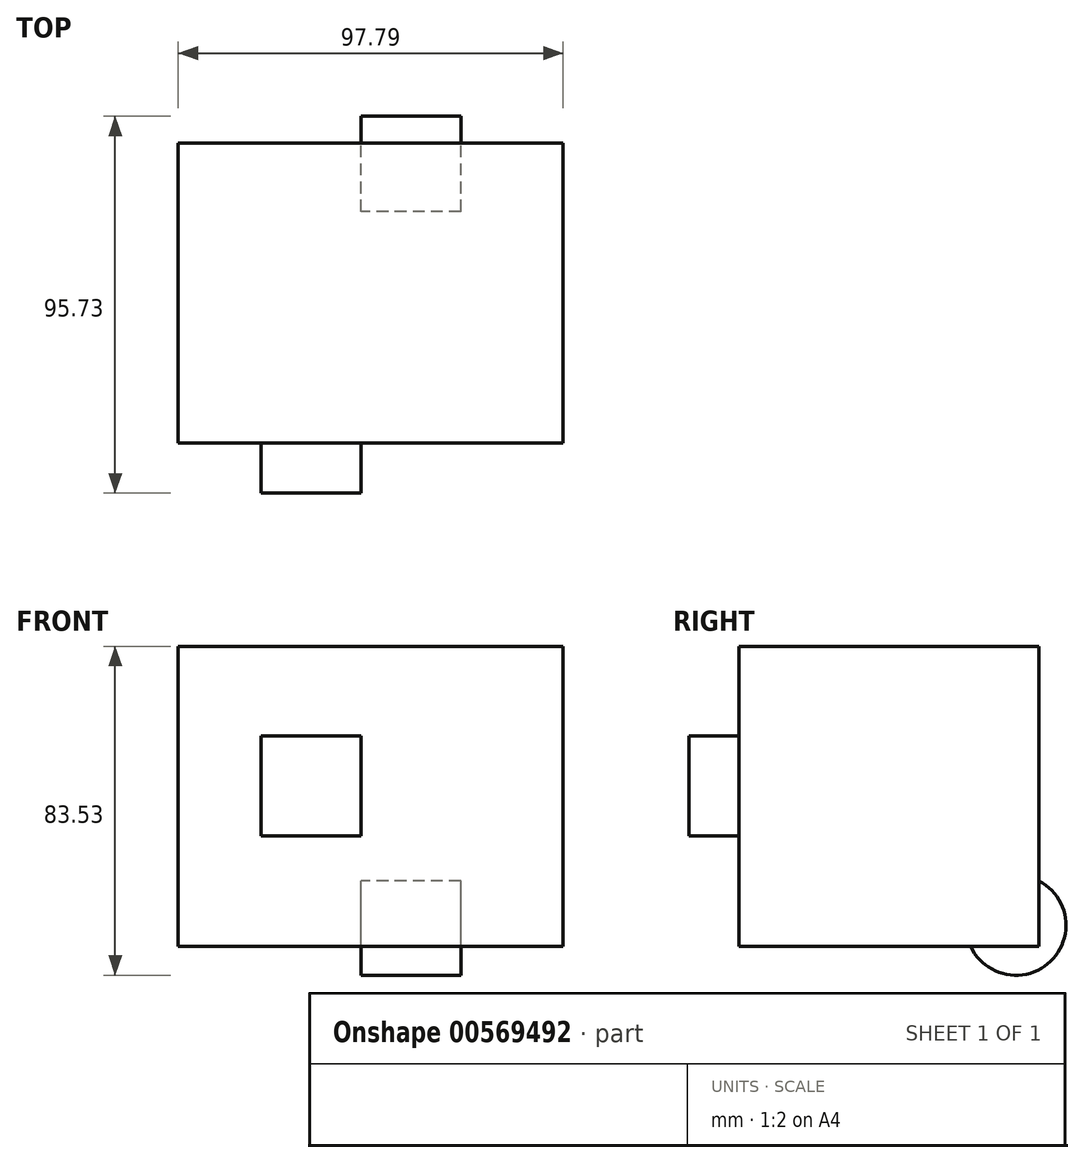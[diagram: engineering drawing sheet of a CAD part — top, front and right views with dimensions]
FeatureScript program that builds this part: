
annotation { "Feature Type Name" : "Feature", "Feature Type Description" : "" }
export const myFeature = defineFeature(function(context is Context, id is Id, definition is map)
    precondition{}
    {
        {
            var Q0;
            Q0=qCreatedBy(makeId("Front.planeOp"),FACE);
            var sketch = newSketch(context, id + "F0", { "sketchPlane" : qUnion([Q0])});
            skLineSegment(sketch, "E0.bottom", {"start": v(-53.9, 110.26) * mm, "end": v(22.3, 110.26) * mm});
            skLineSegment(sketch, "E0.top", {"start": v(-53.9, 34.06) * mm, "end": v(22.3, 34.06) * mm});
            skLineSegment(sketch, "E0.left", {"start": v(-53.9, 110.26) * mm, "end": v(-53.9, 34.06) * mm});
            skLineSegment(sketch, "E0.right", {"start": v(22.3, 110.26) * mm, "end": v(22.3, 34.06) * mm});
            skSolve(sketch);
        }
        {
            var Q0;
            Q0 = qSketchRegion(id + "F0", true);
            extrude(context, id + "F1", {"entities" : qUnion([Q0]), "depth" : 76.2 * mm, "offsetDistance" : 25.4 * mm});
        }
        {
            var Q0;
            Q0=makeQuery(id+"F1.opExtrude","CAP_FACE",FACE,{"disambiguationData":[OSD([sQuery(id+"F0.wireOp",EDGE,"E0.bottom"),sQuery(id+"F0.wireOp",EDGE,"E0.top"),sQuery(id+"F0.wireOp",EDGE,"E0.left"),sQuery(id+"F0.wireOp",EDGE,"E0.right")])],"isStart":false});
            var sketch = newSketch(context, id + "F2", { "sketchPlane" : qUnion([Q0])});
            skLineSegment(sketch, "E1.bottom", {"start": v(-32.92, 87.51) * mm, "end": v(-7.52, 87.51) * mm});
            skLineSegment(sketch, "E1.top", {"start": v(-32.92, 62.11) * mm, "end": v(-7.52, 62.11) * mm});
            skLineSegment(sketch, "E1.left", {"start": v(-32.92, 87.51) * mm, "end": v(-32.92, 62.11) * mm});
            skLineSegment(sketch, "E1.right", {"start": v(-7.52, 87.51) * mm, "end": v(-7.52, 62.11) * mm});
            skSolve(sketch);
        }
        {
            var Q0;
            Q0=makeQuery(id+"F2.imprint","IMPRINT",FACE,{"disambiguationData":[TD([[makeQuery(id+"F2.imprint","IMPRINT",EDGE,{"derivedFrom":sQuery(id+"F2.wireOp",EDGE,"E1.bottom")}),-1.0]])]});
            extrude(context, id + "F3", {"entities" : qUnion([Q0]), "operationType" : NewBodyOperationType.ADD, "depth" : 12.7 * mm, "offsetDistance" : 25.4 * mm});
        }
        {
            var Q0;
            Q0=makeQuery(id+"F3.opExtrude","SWEPT_FACE",FACE,{"disambiguationData":[OSD([sQuery(id+"F2.wireOp",EDGE,"E1.right")])]});
            var sketch = newSketch(context, id + "F4", { "sketchPlane" : qUnion([Q0])});
            skCircle(sketch, "E2", {"center": v(-5.87, 39.43) * mm, "radius": 12.7 * mm});
            skSolve(sketch);
        }
        {
            var Q0;
            Q0 = qSketchRegion(id + "F4", true);
            var Q1;
            Q1=makeQuery(id+"F1.opExtrude","SWEPT_FACE",FACE,{"disambiguationData":[OSD([sQuery(id+"F0.wireOp",EDGE,"E0.right")])]});
            extrude(context, id + "F5", {"entities" : qUnion([Q0, Q1]), "operationType" : NewBodyOperationType.ADD, "depth" : 21.59 * mm, "offsetDistance" : 25.4 * mm});
        }
        {
            var Q0;
            Q0 = qSketchRegion(id + "F4", true);
            extrude(context, id + "F6", {"entities" : qUnion([Q0]), "operationType" : NewBodyOperationType.ADD, "depth" : 25.4 * mm, "offsetDistance" : 25.4 * mm});
        }
    });
